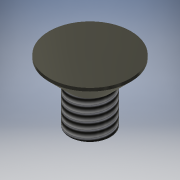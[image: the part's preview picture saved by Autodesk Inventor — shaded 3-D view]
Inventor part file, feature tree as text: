
AUTODESK INVENTOR PART (.ipt)
format: ipt  version: 2016 (Build 200138000, 138)  size: 124,416 bytes
history: native  units: mm
features: extrude x3, sketch x3, other x1, thread x1, chamfer x1
ambient origin geometry x1: Origin
bodies: Body1 (feature_tree)
feature tree (9):
  other  "ソリッド1"
  extrude  "押し出し1"  Depth=4.0mm
  extrude  "押し出し2"  Depth=6.0mm TaperAngle=0.0deg
  thread  "ねじ1"
  extrude  "押し出し3"  Depth=8.0mm
  chamfer  "面取り1"  Distance=2.3mm
  sketch  "スケッチ1"
  sketch  "スケッチ2"
  sketch  "スケッチ3"
